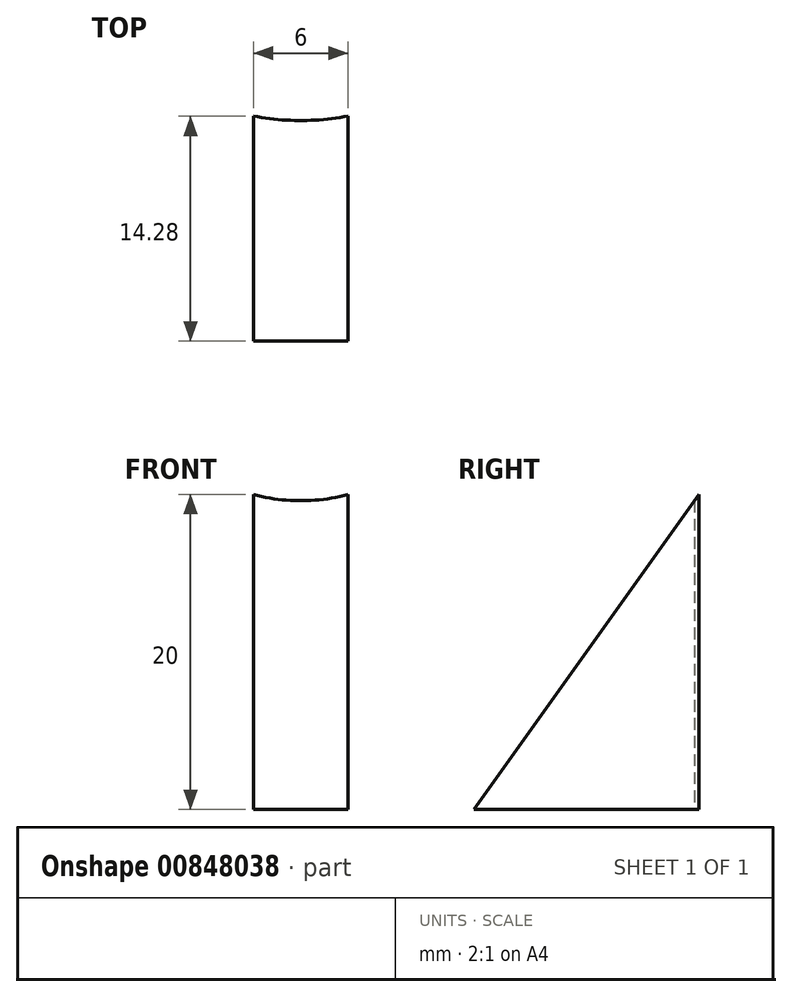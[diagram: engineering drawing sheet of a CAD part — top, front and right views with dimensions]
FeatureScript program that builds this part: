
annotation { "Feature Type Name" : "Feature", "Feature Type Description" : "" }
export const myFeature = defineFeature(function(context is Context, id is Id, definition is map)
    precondition{}
    {
        {
            var Q0;
            Q0=qCreatedBy(makeId("Top.planeOp"),FACE);
            var sketch = newSketch(context, id + "F0", { "sketchPlane" : qUnion([Q0])});
            skLineSegment(sketch, "E0.bottom", {"start": v(3, -10) * mm, "end": v(-3, -10) * mm});
            skLineSegment(sketch, "E0.top", {"start": v(3, 10) * mm, "end": v(-3, 10) * mm});
            skLineSegment(sketch, "E0.left", {"start": v(3, -10) * mm, "end": v(3, 10) * mm});
            skLineSegment(sketch, "E0.right", {"start": v(-3, -10) * mm, "end": v(-3, 10) * mm});
            skPoint(sketch, "E0.middle", {"position": v(0, 0) * mm});
            skLineSegment(sketch, "E1", {"start": v(0, -10) * mm, "end": v(0, 20) * mm, "construction": true});
            skCircle(sketch, "E2", {"center": v(0, 20) * mm, "radius": 16 * mm});
            skSolve(sketch);
        }
        {
            var Q0;
            {var subQ0=sQuery(id+"F0.wireOp",EDGE,"E0.bottom");Q0=makeQuery(id+"F0.imprint","IMPRINT",FACE,{"disambiguationData":[TD([[makeQuery(id+"F0.imprint","IMPRINT",EDGE,{"derivedFrom":subQ0}),-1.0]])]});}
            extrude(context, id + "F1", {"entities" : qUnion([Q0]), "depth" : 20 * mm, "offsetDistance" : 25 * mm});
        }
        {
            var Q0;
            Q0=makeQuery(id+"F1.opExtrude","CAP_EDGE",EDGE,{"disambiguationData":[OSD([sQuery(id+"F0.wireOp",EDGE,"E0.bottom")])],"isStart":false});
            chamfer(context, id + "F2", {"entities" : qUnion([Q0]), "chamferType" : ChamferType.TWO_OFFSETS, "width1" : 20 * mm, "oppositeDirection" : false, "width2" : 14.28 * mm, "tangentPropagation" : true});
        }
    });
